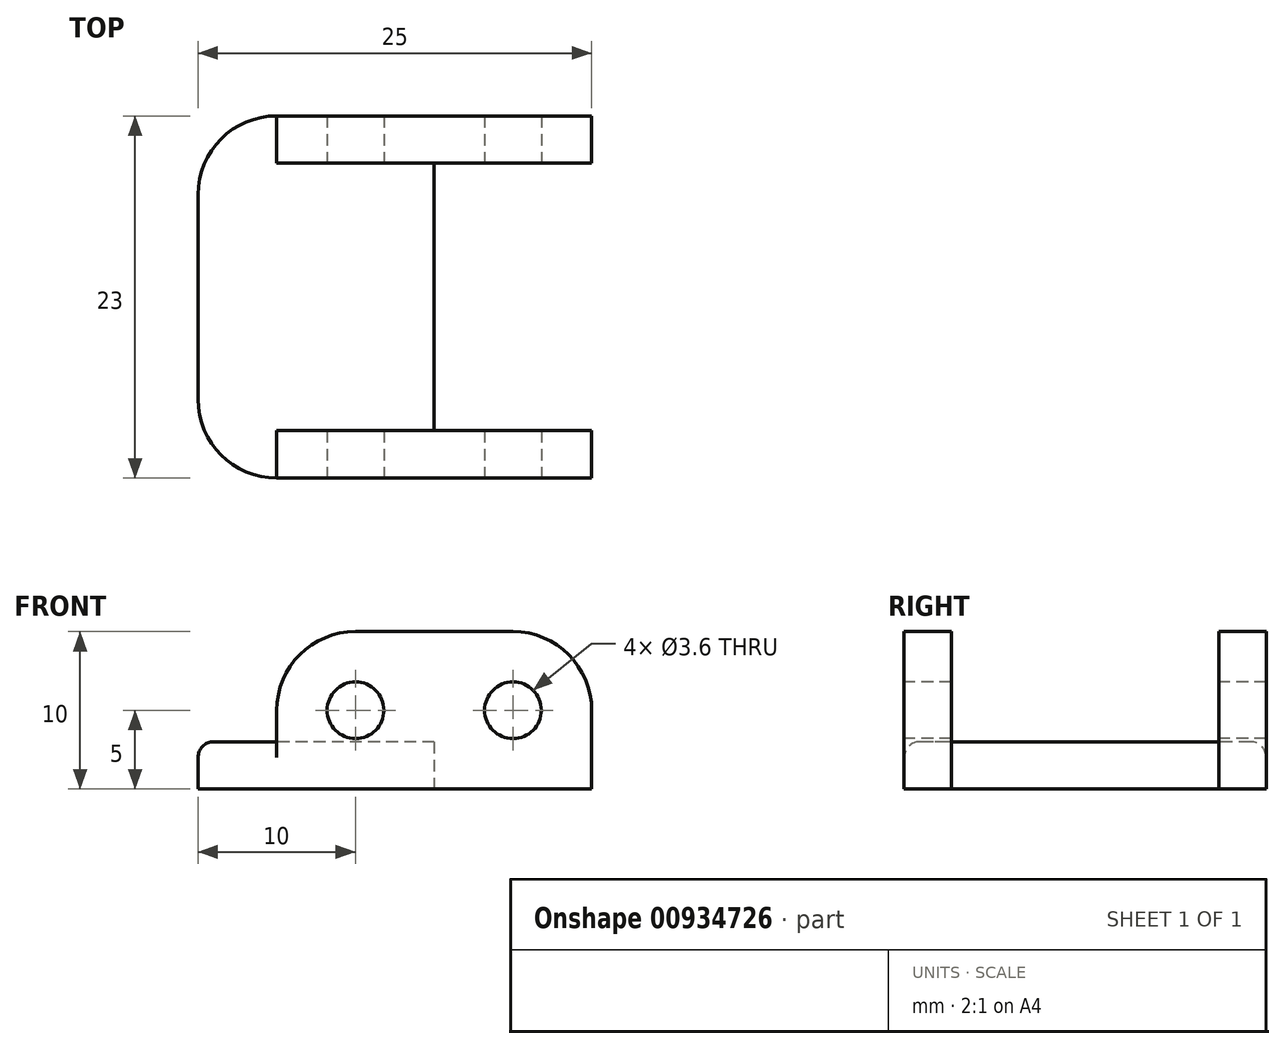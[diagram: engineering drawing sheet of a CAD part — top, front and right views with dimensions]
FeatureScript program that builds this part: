
annotation { "Feature Type Name" : "Feature", "Feature Type Description" : "" }
export const myFeature = defineFeature(function(context is Context, id is Id, definition is map)
    precondition{}
    {
        {
            var Q0;
            Q0=qCreatedBy(makeId("Top.planeOp"),FACE);
            var sketch = newSketch(context, id + "F0", { "sketchPlane" : qUnion([Q0])});
            skLineSegment(sketch, "E0.top", {"start": v(-7.9, -6) * mm, "end": v(17.1, -6) * mm});
            skLineSegment(sketch, "E0.left", {"start": v(-7.9, 17) * mm, "end": v(-7.9, -6) * mm});
            skLineSegment(sketch, "E1", {"start": v(17.1, -6) * mm, "end": v(17.1, -3) * mm});
            skLineSegment(sketch, "E2", {"start": v(17.1, -3) * mm, "end": v(7.1, -3) * mm});
            skLineSegment(sketch, "E3", {"start": v(7.1, -3) * mm, "end": v(7.1, 14) * mm});
            skLineSegment(sketch, "E4", {"start": v(7.1, 14) * mm, "end": v(17.1, 14) * mm});
            skLineSegment(sketch, "E5", {"start": v(17.1, 14) * mm, "end": v(17.1, 17) * mm});
            skLineSegment(sketch, "E6", {"start": v(-7.9, 17) * mm, "end": v(17.1, 17) * mm});
            skSolve(sketch);
        }
        {
            var Q0;
            Q0 = qSketchRegion(id + "F0", true);
            extrude(context, id + "F1", {"entities" : qUnion([Q0]), "depth" : 3 * mm, "offsetDistance" : 25 * mm});
        }
        {
            var Q0;
            Q0=makeQuery(id+"F1.opExtrude","CAP_FACE",FACE,{"disambiguationData":[OSD([sQuery(id+"F0.wireOp",EDGE,"E0.top"),sQuery(id+"F0.wireOp",EDGE,"E0.left"),sQuery(id+"F0.wireOp",EDGE,"E1"),sQuery(id+"F0.wireOp",EDGE,"E2"),sQuery(id+"F0.wireOp",EDGE,"E3"),sQuery(id+"F0.wireOp",EDGE,"E4"),sQuery(id+"F0.wireOp",EDGE,"E5"),sQuery(id+"F0.wireOp",EDGE,"E6")])],"isStart":false});
            var sketch = newSketch(context, id + "F2", { "sketchPlane" : qUnion([Q0])});
            skLineSegment(sketch, "E7.bottom", {"start": v(17.1, 17) * mm, "end": v(-2.9, 17) * mm});
            skLineSegment(sketch, "E7.top", {"start": v(17.1, 14) * mm, "end": v(-2.9, 14) * mm});
            skLineSegment(sketch, "E7.left", {"start": v(17.1, 17) * mm, "end": v(17.1, 14) * mm});
            skLineSegment(sketch, "E7.right", {"start": v(-2.9, 17) * mm, "end": v(-2.9, 14) * mm});
            skLineSegment(sketch, "E8.bottom", {"start": v(17.1, -3) * mm, "end": v(-2.9, -3) * mm});
            skLineSegment(sketch, "E8.top", {"start": v(17.1, -6) * mm, "end": v(-2.9, -6) * mm});
            skLineSegment(sketch, "E8.left", {"start": v(17.1, -3) * mm, "end": v(17.1, -6) * mm});
            skLineSegment(sketch, "E8.right", {"start": v(-2.9, -3) * mm, "end": v(-2.9, -6) * mm});
            skSolve(sketch);
        }
        {
            var Q0;
            Q0 = qSketchRegion(id + "F2", true);
            extrude(context, id + "F3", {"entities" : qUnion([Q0]), "operationType" : NewBodyOperationType.ADD, "depth" : 7 * mm, "offsetDistance" : 25 * mm});
        }
        {
            var Q0;
            Q0=makeQuery(id+"F1.opExtrude","SWEPT_EDGE",EDGE,{"disambiguationData":[OSD([sQuery(id+"F0.wireOp",EDGE,"E0.left"),sQuery(id+"F0.wireOp",EDGE,"E6")])]});
            var Q1;
            Q1=makeQuery(id+"F1.opExtrude","SWEPT_EDGE",EDGE,{"disambiguationData":[OSD([sQuery(id+"F0.wireOp",EDGE,"E0.top"),sQuery(id+"F0.wireOp",EDGE,"E0.left")])]});
            var Q2;
            Q2=makeQuery(id+"F3.opExtrude","CAP_EDGE",EDGE,{"disambiguationData":[OSD([sQuery(id+"F2.wireOp",EDGE,"E8.right")])],"isStart":false});
            var Q3;
            Q3=makeQuery(id+"F3.opExtrude","CAP_EDGE",EDGE,{"disambiguationData":[OSD([sQuery(id+"F2.wireOp",EDGE,"E7.right")])],"isStart":false});
            fillet(context, id + "F4", {"entities" : qUnion([Q0, Q1, Q2, Q3]), "radius" : 5 * mm, "tangentPropagation" : true, "allowEdgeOverflow" : false});
        }
        {
            var Q0;
            Q0=makeQuery(id+"F3.opExtrude","CAP_EDGE",EDGE,{"disambiguationData":[OSD([sQuery(id+"F2.wireOp",EDGE,"E7.left")])],"isStart":false});
            var Q1;
            Q1=makeQuery(id+"F3.opExtrude","CAP_EDGE",EDGE,{"disambiguationData":[OSD([sQuery(id+"F2.wireOp",EDGE,"E8.left")])],"isStart":false});
            fillet(context, id + "F5", {"entities" : qUnion([Q0, Q1]), "radius" : 5 * mm, "tangentPropagation" : true, "allowEdgeOverflow" : false});
        }
        {
            var Q0;
            {var subQ0=sQuery(id+"F0.wireOp",EDGE,"E6");var subQ1=sQuery(id+"F0.wireOp",EDGE,"E0.left");Q0=makeQuery(id+"F4.opFillet","BLEND_EDGE",EDGE,{"blendedFrom":[makeQuery(id+"F1.opExtrude","SWEPT_EDGE",EDGE,{"disambiguationData":[OSD([subQ1,subQ0])]}),makeQuery(id+"F1.opExtrude","CAP_FACE",FACE,{"disambiguationData":[OSD([sQuery(id+"F0.wireOp",EDGE,"E0.top"),subQ1,sQuery(id+"F0.wireOp",EDGE,"E1"),sQuery(id+"F0.wireOp",EDGE,"E2"),sQuery(id+"F0.wireOp",EDGE,"E3"),sQuery(id+"F0.wireOp",EDGE,"E4"),sQuery(id+"F0.wireOp",EDGE,"E5"),subQ0])],"isStart":false})],"blendedInto":[makeQuery(id+"F1.opExtrude","CAP_FACE",FACE,{"disambiguationData":[OSD([sQuery(id+"F0.wireOp",EDGE,"E0.top"),subQ1,sQuery(id+"F0.wireOp",EDGE,"E1"),sQuery(id+"F0.wireOp",EDGE,"E2"),sQuery(id+"F0.wireOp",EDGE,"E3"),sQuery(id+"F0.wireOp",EDGE,"E4"),sQuery(id+"F0.wireOp",EDGE,"E5"),subQ0])],"isStart":false})]});}
            var Q1;
            Q1=makeQuery(id+"F1.opExtrude","CAP_EDGE",EDGE,{"disambiguationData":[OSD([sQuery(id+"F0.wireOp",EDGE,"E0.left")])],"isStart":false});
            var Q2;
            {var subQ0=sQuery(id+"F0.wireOp",EDGE,"E0.left");var subQ1=sQuery(id+"F0.wireOp",EDGE,"E0.top");Q2=makeQuery(id+"F4.opFillet","BLEND_EDGE",EDGE,{"blendedFrom":[makeQuery(id+"F1.opExtrude","SWEPT_EDGE",EDGE,{"disambiguationData":[OSD([subQ1,subQ0])]}),makeQuery(id+"F1.opExtrude","CAP_FACE",FACE,{"disambiguationData":[OSD([subQ1,subQ0,sQuery(id+"F0.wireOp",EDGE,"E1"),sQuery(id+"F0.wireOp",EDGE,"E2"),sQuery(id+"F0.wireOp",EDGE,"E3"),sQuery(id+"F0.wireOp",EDGE,"E4"),sQuery(id+"F0.wireOp",EDGE,"E5"),sQuery(id+"F0.wireOp",EDGE,"E6")])],"isStart":false})],"blendedInto":[makeQuery(id+"F1.opExtrude","CAP_FACE",FACE,{"disambiguationData":[OSD([subQ1,subQ0,sQuery(id+"F0.wireOp",EDGE,"E1"),sQuery(id+"F0.wireOp",EDGE,"E2"),sQuery(id+"F0.wireOp",EDGE,"E3"),sQuery(id+"F0.wireOp",EDGE,"E4"),sQuery(id+"F0.wireOp",EDGE,"E5"),sQuery(id+"F0.wireOp",EDGE,"E6")])],"isStart":false})]});}
            fillet(context, id + "F6", {"entities" : qUnion([Q0, Q1, Q2]), "radius" : 1 * mm, "tangentPropagation" : true, "allowEdgeOverflow" : false});
        }
        {
            var Q0;
            Q0=makeQuery(id+"F3.boolean.opBoolean","MERGE",FACE,{"derivedFrom":[makeQuery(id+"F1.opExtrude","SWEPT_FACE",FACE,{"disambiguationData":[OSD([sQuery(id+"F0.wireOp",EDGE,"E0.top")])]}),makeQuery(id+"F3.opExtrude","SWEPT_FACE",FACE,{"disambiguationData":[OSD([sQuery(id+"F2.wireOp",EDGE,"E8.top")])]})]});
            var sketch = newSketch(context, id + "F7", { "sketchPlane" : qUnion([Q0])});
            skLineSegment(sketch, "E9.bottom", {"start": v(17.1, 0) * mm, "end": v(2.1, 0) * mm, "construction": true});
            skLineSegment(sketch, "E9.top", {"start": v(17.1, 10) * mm, "end": v(2.1, 10) * mm, "construction": true});
            skLineSegment(sketch, "E9.left", {"start": v(17.1, 0) * mm, "end": v(17.1, 10) * mm, "construction": true});
            skLineSegment(sketch, "E10.bottom", {"start": v(-2.9, 0) * mm, "end": v(2.1, 0) * mm, "construction": true});
            skLineSegment(sketch, "E10.top", {"start": v(-2.9, 10) * mm, "end": v(2.1, 10) * mm, "construction": true});
            skLineSegment(sketch, "E10.left", {"start": v(-2.9, 0) * mm, "end": v(-2.9, 10) * mm, "construction": true});
            skCircle(sketch, "E11", {"center": v(12.1, 5) * mm, "radius": 1.8 * mm});
            skCircle(sketch, "E12", {"center": v(2.1, 5) * mm, "radius": 1.8 * mm});
            skSolve(sketch);
        }
        {
            var Q0;
            Q0 = qSketchRegion(id + "F7", true);
            extrude(context, id + "F8", {"entities" : qUnion([Q0]), "operationType" : NewBodyOperationType.REMOVE, "oppositeDirection" : true, "depth" : 24 * mm, "offsetDistance" : 25 * mm});
        }
    });
